# Revit family: Projector_Screen-Ultimate_Access_XL_Series_V
name_source: partatom
category: Specialty Equipment
units: mm (PartAtom-declared; Revit-internal decimal feet)

## family parameters
Classification Number = 23.85.10.14.31
Cut with Voids When Loaded = No
Enable Cutting in Views = No
Host = Face
Maintain Annotation Orientation = No
Part Type = Normal
Room Calculation Point = No
Round Connector Dimension = Use Diameter
Shared = No

## types (1)
- NOT A TYPE - LOAD TYPE CATALOG
    Apparent Load = 132 VA
    Case Material = Paint - Draper - White
    Default Elevation = 4' - 0"
    Description = Projection Screen
    Frequency = 60 Hz
    Image Area = 126” x 168”
    Image Height = 10' - 6"
    Image Height Constraint = 10' - 6"
    Image Length = 14' - 0"
    Image Length Constraint = 14' - 0"
    Length = 16' - 4 7/8"
    Manufacturer = Draper Inc.
    Model = Ultimate Access XL
    Number of Poles = 1
    Overall Size = 126" x 168"
    Power Factor = 1
    Product Documentation Link = http://www.draperinc.com
    Product Name = Ultimate Access XL/Series V Electric Projection Screen
    Product Page URL = http://www.draperinc.com
    Projection Screen Material = Fabric - Draper - XH1500E - Argent White
    Screen = 14' - 7"
    Screen Drop = 11' - 6"
    URL = http://www.draperinc.com
    Version = 2013 – v1.0a
    Voltage = 110 V
    Width = 9 1/2"

## geometry (parser evidence)
native form markers: Blend x8, Sweep x6
no freeform markers — native parametric forms only
